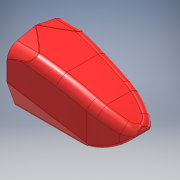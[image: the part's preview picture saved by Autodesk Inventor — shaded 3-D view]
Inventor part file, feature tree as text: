
AUTODESK INVENTOR PART (.ipt)
format: ipt  version: 2018 (Build 220112000, 112)  size: 2,074,624 bytes
history: native  units: mm
features: other x1, shell x1
ambient origin geometry x8: Origin, YZ Plane, XZ Plane, XY Plane, X Axis, Y Axis, Z Axis, Center Point
bodies: Body1 (feature_tree)
feature tree (2):
  other  "ソリッド1"
  shell  "シェル1"  Thickness=3.0mm
